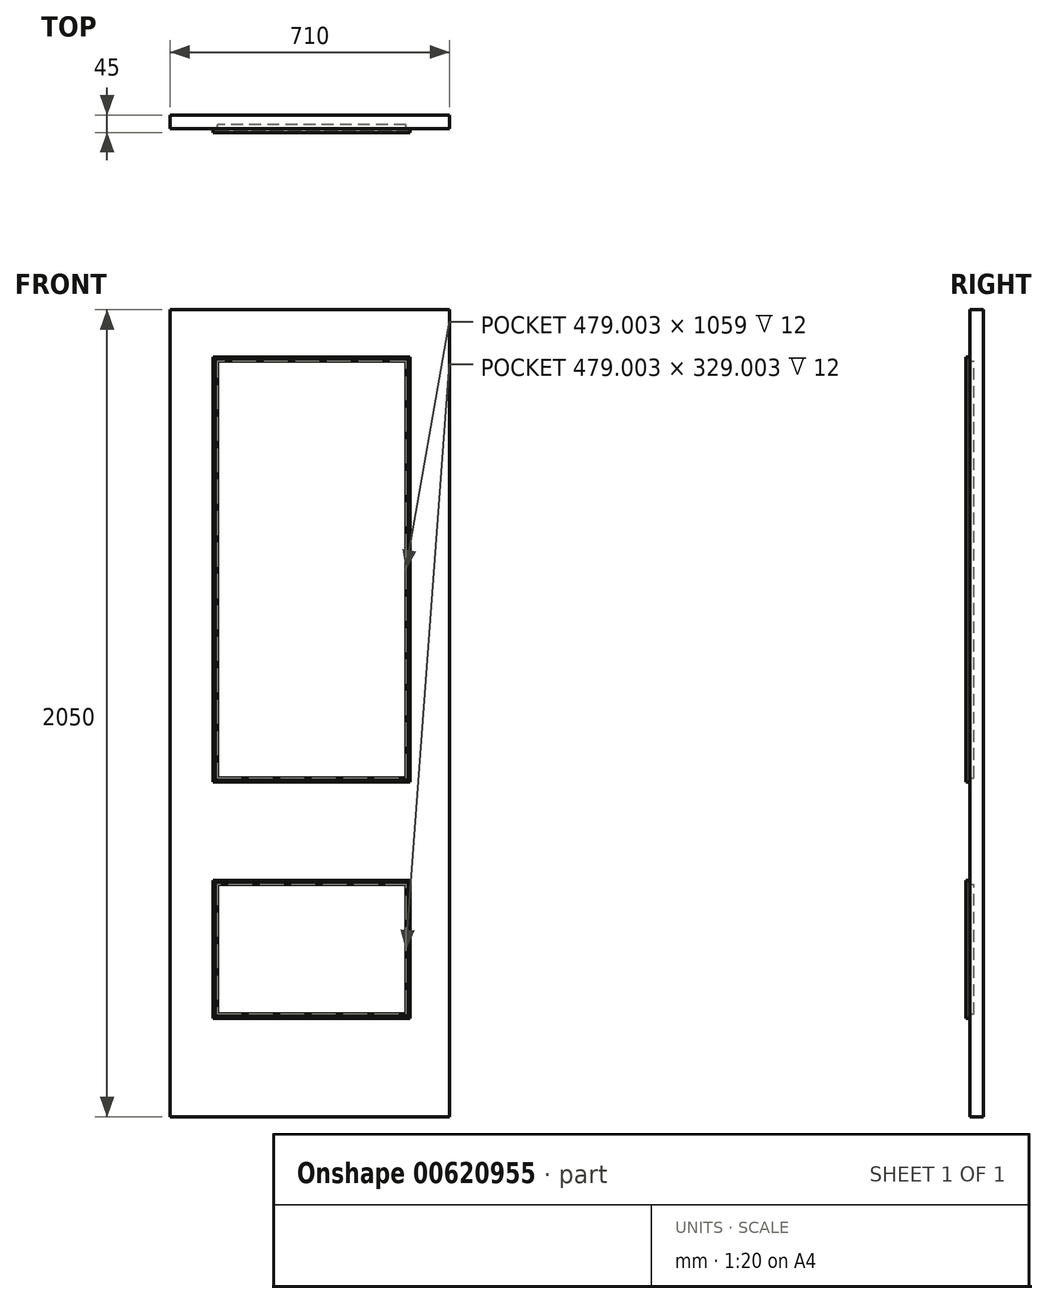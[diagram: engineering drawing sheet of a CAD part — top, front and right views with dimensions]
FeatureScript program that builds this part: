
annotation { "Feature Type Name" : "Feature", "Feature Type Description" : "" }
export const myFeature = defineFeature(function(context is Context, id is Id, definition is map)
    precondition{}
    {
        {
            var Q0;
            Q0=qCreatedBy(makeId("Top.planeOp"),FACE);
            var sketch = newSketch(context, id + "F0", { "sketchPlane" : qUnion([Q0])});
            skLineSegment(sketch, "E0.bottom", {"start": v(-355, 0) * mm, "end": v(355, 0) * mm});
            skLineSegment(sketch, "E0.top", {"start": v(-355, 35) * mm, "end": v(355, 35) * mm});
            skLineSegment(sketch, "E0.left", {"start": v(-355, 0) * mm, "end": v(-355, 35) * mm});
            skLineSegment(sketch, "E0.right", {"start": v(355, 0) * mm, "end": v(355, 35) * mm});
            skSolve(sketch);
        }
        {
            var Q0;
            Q0 = qSketchRegion(id + "F0", true);
            extrude(context, id + "F1", {"entities" : qUnion([Q0]), "depth" : 2050 * mm, "offsetDistance" : 25 * mm});
        }
        {
            var Q0;
            Q0=makeQuery(id+"F1.opExtrude","SWEPT_FACE",FACE,{"disambiguationData":[OSD([sQuery(id+"F0.wireOp",EDGE,"E0.bottom")])]});
            var sketch = newSketch(context, id + "F2", { "sketchPlane" : qUnion([Q0])});
            skLineSegment(sketch, "E1.bottom", {"start": v(-245, 250) * mm, "end": v(255, 250) * mm});
            skLineSegment(sketch, "E1.top", {"start": v(-245, 600) * mm, "end": v(255, 600) * mm});
            skLineSegment(sketch, "E1.left", {"start": v(-245, 250) * mm, "end": v(-245, 600) * mm});
            skLineSegment(sketch, "E1.right", {"start": v(255, 250) * mm, "end": v(255, 600) * mm});
            skLineSegment(sketch, "E2.bottom", {"start": v(-245, 850) * mm, "end": v(255, 850) * mm});
            skLineSegment(sketch, "E2.top", {"start": v(-245, 1930) * mm, "end": v(255, 1930) * mm});
            skLineSegment(sketch, "E2.left", {"start": v(-245, 850) * mm, "end": v(-245, 1930) * mm});
            skLineSegment(sketch, "E2.right", {"start": v(255, 850) * mm, "end": v(255, 1930) * mm});
            skSolve(sketch);
        }
        {
            var Q0;
            Q0 = qSketchRegion(id + "F2", true);
            extrude(context, id + "F3", {"entities" : qUnion([Q0]), "operationType" : NewBodyOperationType.REMOVE, "oppositeDirection" : true, "depth" : 10 * mm, "offsetDistance" : 25 * mm});
        }
        {
            var Q0;
            Q0=qCreatedBy(makeId("Right.planeOp"),FACE);
            var sketch = newSketch(context, id + "F4", { "sketchPlane" : qUnion([Q0])});
            skLineSegment(sketch, "E3", {"start": v(10, 850) * mm, "end": v(-10, 850) * mm});
            skLineSegment(sketch, "E4", {"start": v(-10, 850) * mm, "end": v(-10, 853) * mm});
            skLineSegment(sketch, "E5", {"start": v(-10, 853) * mm, "end": v(-8, 853) * mm});
            skArc(sketch, "E6", {"start": v(-5.93, 855) * mm, "mid": v(-7.39, 854.44) * mm, "end": v(-8, 853) * mm});
            skLineSegment(sketch, "E7", {"start": v(-5.93, 855) * mm, "end": v(-5.93, 857.5) * mm});
            skLineSegment(sketch, "E8", {"start": v(-5.93, 857.5) * mm, "end": v(-2, 857.5) * mm});
            skLineSegment(sketch, "E9", {"start": v(-2, 857.5) * mm, "end": v(-2, 860.5) * mm});
            skLineSegment(sketch, "E10", {"start": v(-2, 860.5) * mm, "end": v(10, 860.5) * mm});
            skPoint(sketch, "E11.orphan", {"position": v(0, 860.5) * mm});
            skPoint(sketch, "E12.orphan", {"position": v(0, 850) * mm});
            skLineSegment(sketch, "E13", {"start": v(10, 860.5) * mm, "end": v(10, 850) * mm});
            skSolve(sketch);
        }
        {
            var Q0;
            Q0=makeQuery(id+"F3.boolean.opBoolean","COPY",FACE,{"derivedFrom":makeQuery(id+"F3.opExtrude","CAP_FACE",FACE,{"disambiguationData":[OSD([sQuery(id+"F2.wireOp",EDGE,"E2.bottom"),sQuery(id+"F2.wireOp",EDGE,"E2.top"),sQuery(id+"F2.wireOp",EDGE,"E2.left"),sQuery(id+"F2.wireOp",EDGE,"E2.right")])],"isStart":false})});
            var sketch = newSketch(context, id + "F5", { "sketchPlane" : qUnion([Q0])});
            skLineSegment(sketch, "E14.0.0", {"start": v(255, 1930) * mm, "end": v(-245, 1930) * mm});
            skLineSegment(sketch, "E14.0.1", {"start": v(-245, 1930) * mm, "end": v(-245, 850) * mm});
            skLineSegment(sketch, "E14.0.2", {"start": v(-245, 850) * mm, "end": v(255, 850) * mm});
            skLineSegment(sketch, "E14.0.3", {"start": v(255, 850) * mm, "end": v(255, 1930) * mm});
            skSolve(sketch);
        }
        {
            var Q0;
            Q0=makeQuery(id+"F4.imprint","IMPRINT",FACE,{"disambiguationData":[TD([[makeQuery(id+"F4.imprint","IMPRINT",EDGE,{"derivedFrom":sQuery(id+"F4.wireOp",EDGE,"E3")}),-1.0]])]});
            var Q1;
            Q1 = qConstructionFilter(qBodyType(qCreatedBy(id + "F5" ,EDGE), BodyType.WIRE), ConstructionObject.NO);
            sweep(context, id + "F6", {"operationType" : NewBodyOperationType.ADD, "profiles" : qUnion([Q0]), "path" : qUnion([Q1])});
        }
        {
            var Q0;
            Q0=qCreatedBy(makeId("Right.planeOp"),FACE);
            var sketch = newSketch(context, id + "F7", { "sketchPlane" : qUnion([Q0])});
            skLineSegment(sketch, "E15", {"start": v(10, 250) * mm, "end": v(-10, 250) * mm});
            skLineSegment(sketch, "E16", {"start": v(-10, 250) * mm, "end": v(-10, 253) * mm});
            skLineSegment(sketch, "E17", {"start": v(-10, 253) * mm, "end": v(-8, 253) * mm});
            skArc(sketch, "E18", {"start": v(-5.93, 255) * mm, "mid": v(-7.39, 254.44) * mm, "end": v(-8, 253) * mm});
            skLineSegment(sketch, "E19", {"start": v(-5.93, 255) * mm, "end": v(-5.93, 257.5) * mm});
            skLineSegment(sketch, "E20", {"start": v(-5.93, 257.5) * mm, "end": v(-2, 257.5) * mm});
            skLineSegment(sketch, "E21", {"start": v(-2, 257.5) * mm, "end": v(-2, 260.5) * mm});
            skLineSegment(sketch, "E22", {"start": v(-2, 260.5) * mm, "end": v(10, 260.5) * mm});
            skPoint(sketch, "E23.orphan", {"position": v(2.2, 260.5) * mm});
            skPoint(sketch, "E24.orphan", {"position": v(2.2, 250) * mm});
            skLineSegment(sketch, "E25", {"start": v(10, 260.5) * mm, "end": v(10, 250) * mm});
            skSolve(sketch);
        }
        {
            var Q0;
            Q0=makeQuery(id+"F3.boolean.opBoolean","COPY",FACE,{"derivedFrom":makeQuery(id+"F3.opExtrude","CAP_FACE",FACE,{"disambiguationData":[OSD([sQuery(id+"F2.wireOp",EDGE,"E1.bottom"),sQuery(id+"F2.wireOp",EDGE,"E1.top"),sQuery(id+"F2.wireOp",EDGE,"E1.left"),sQuery(id+"F2.wireOp",EDGE,"E1.right")])],"isStart":false})});
            var sketch = newSketch(context, id + "F8", { "sketchPlane" : qUnion([Q0])});
            skLineSegment(sketch, "E26.0.0", {"start": v(255, 600) * mm, "end": v(-245, 600) * mm});
            skLineSegment(sketch, "E26.0.1", {"start": v(-245, 600) * mm, "end": v(-245, 250) * mm});
            skLineSegment(sketch, "E26.0.2", {"start": v(-245, 250) * mm, "end": v(255, 250) * mm});
            skLineSegment(sketch, "E26.0.3", {"start": v(255, 250) * mm, "end": v(255, 600) * mm});
            skSolve(sketch);
        }
        {
            var Q0;
            Q0 = qSketchRegion(id + "F7", true);
            var Q1;
            Q1 = qConstructionFilter(qBodyType(qCreatedBy(id + "F8" ,EDGE), BodyType.WIRE), ConstructionObject.NO);
            sweep(context, id + "F9", {"operationType" : NewBodyOperationType.ADD, "profiles" : qUnion([Q0]), "path" : qUnion([Q1])});
        }
    });
